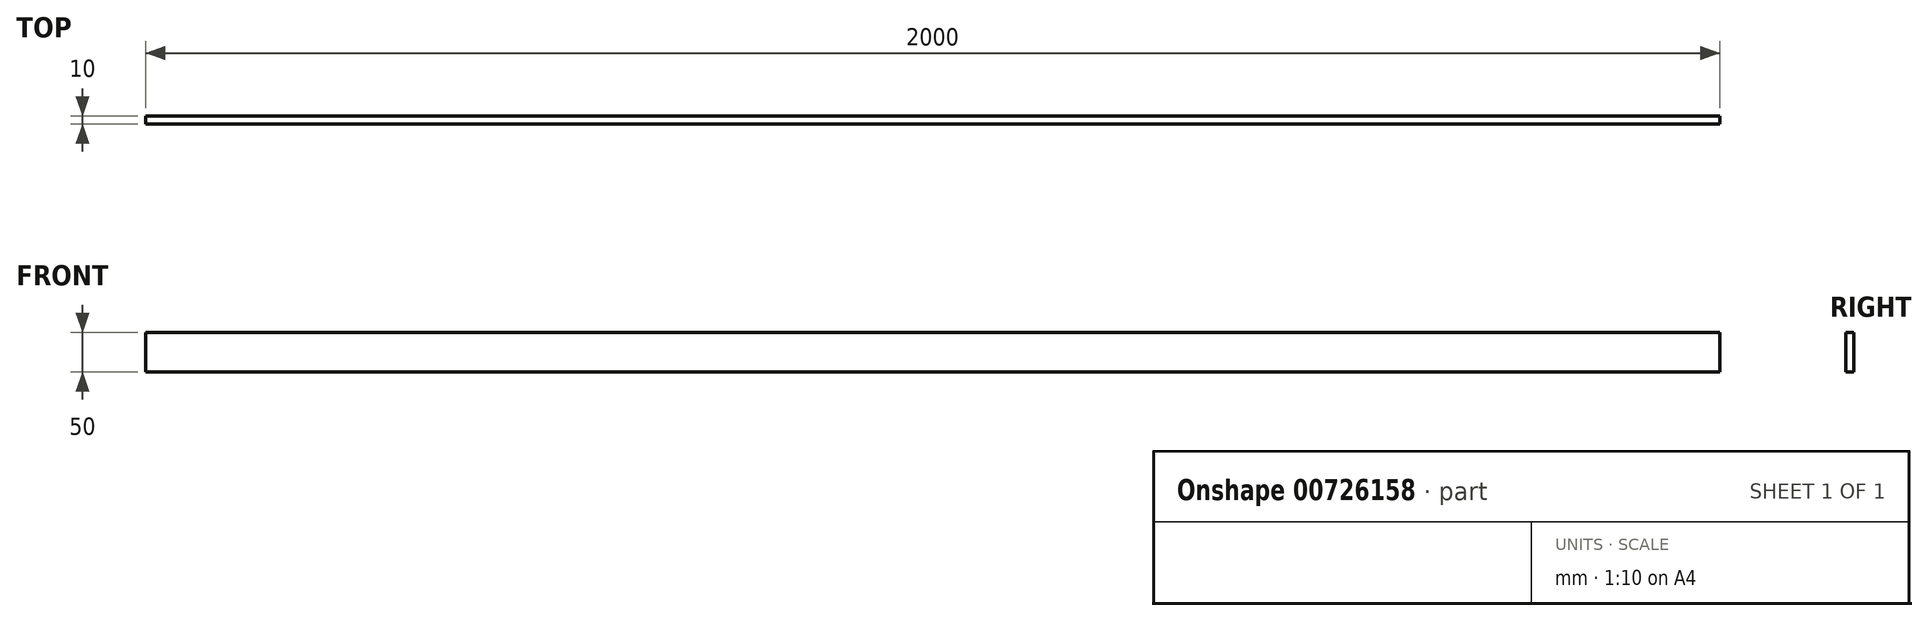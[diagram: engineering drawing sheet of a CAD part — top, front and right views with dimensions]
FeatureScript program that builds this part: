
annotation { "Feature Type Name" : "Feature", "Feature Type Description" : "" }
export const myFeature = defineFeature(function(context is Context, id is Id, definition is map)
    precondition{}
    {
        {
            var Q0;
            Q0=qCreatedBy(makeId("Front.planeOp"),FACE);
            var sketch = newSketch(context, id + "F0", { "sketchPlane" : qUnion([Q0])});
            skLineSegment(sketch, "E0.bottom", {"start": v(-1000, 25) * mm, "end": v(1000, 25) * mm});
            skLineSegment(sketch, "E0.top", {"start": v(-1000, -25) * mm, "end": v(1000, -25) * mm});
            skLineSegment(sketch, "E0.left", {"start": v(-1000, 25) * mm, "end": v(-1000, -25) * mm});
            skLineSegment(sketch, "E0.right", {"start": v(1000, 25) * mm, "end": v(1000, -25) * mm});
            skLineSegment(sketch, "E1", {"start": v(0, -25) * mm, "end": v(0, 25) * mm, "construction": true});
            skSolve(sketch);
        }
        {
            var Q0;
            Q0 = qSketchRegion(id + "F0", true);
            extrude(context, id + "F1", {"entities" : qUnion([Q0]), "depth" : 10 * mm, "offsetDistance" : 25 * mm});
        }
    });
